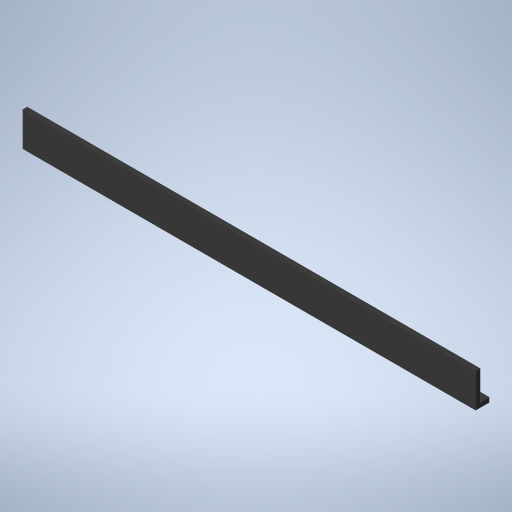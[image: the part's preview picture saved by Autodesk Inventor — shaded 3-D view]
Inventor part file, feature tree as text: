
AUTODESK INVENTOR PART (.ipt)
format: ipt  version: 2024.3 (Build 283343000, 343)  size: 233,472 bytes
history: native  units: mm
features: extrude x1, sketch x1
ambient origin geometry x8: Origin, YZ Plane, XZ Plane, XY Plane, X Axis, Y Axis, Z Axis, Center Point
bodies: Solid1 (feature_tree)
feature tree (2):
  extrude  "Extrusion1"  Depth=2.0mm
  sketch  "Sketch1"  dims[d0=15.0mm d1=2.0mm d2=2.0mm d3=6.0mm d4=200.0mm d5=0.0mm]
